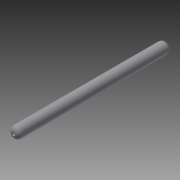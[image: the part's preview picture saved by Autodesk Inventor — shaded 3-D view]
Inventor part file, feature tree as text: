
AUTODESK INVENTOR PART (.ipt)
format: ipt  version: 2013 (Build 170138000, 138)  size: 82,432 bytes
history: native  units: in
note: dims shown in document units (in); Inventor stores cm internally (conversion verified against a paired STEP export)
features: extrude x1, fillet x1, sketch x1
ambient origin geometry x8: Origin, YZ Plane, XZ Plane, XY Plane, X Axis, Y Axis, Z Axis, Center Point
bodies: Solid1 (feature_tree)
feature tree (3):
  extrude  "Extrusion1"  Depth=0.75in
  fillet  "Fillet1"  Radius=33.875in
  sketch  "Sketch1"  dims[d0=2.5in d1=0.75in d2=33.875in d3=0.0in d4=1.0in]
